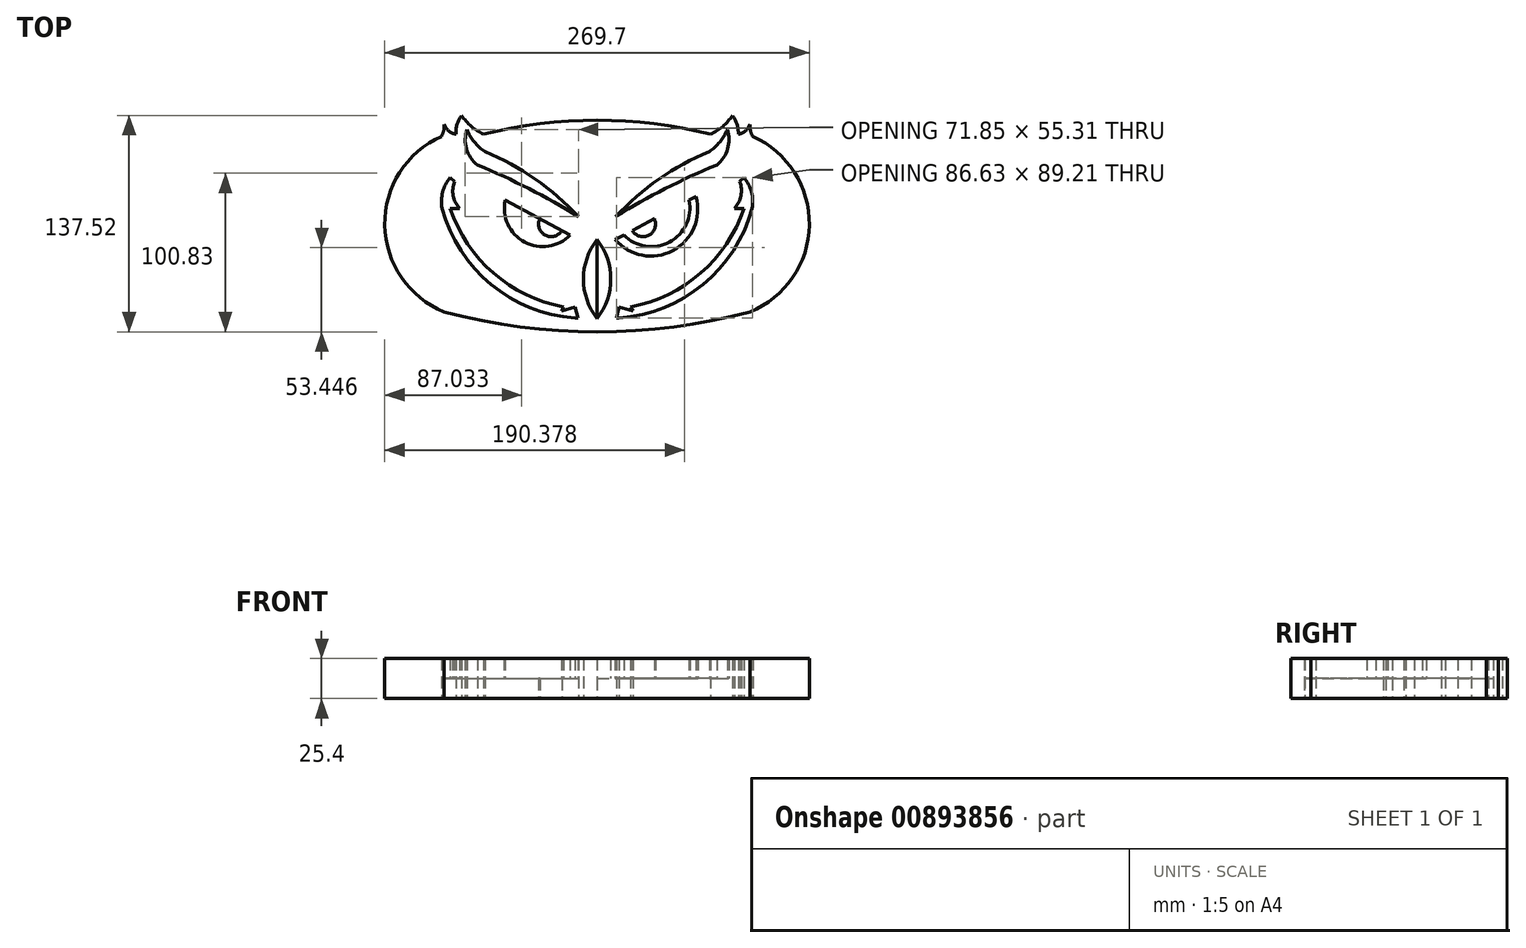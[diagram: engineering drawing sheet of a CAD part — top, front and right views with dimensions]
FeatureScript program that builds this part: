
annotation { "Feature Type Name" : "Feature", "Feature Type Description" : "" }
export const myFeature = defineFeature(function(context is Context, id is Id, definition is map)
    precondition{}
    {
        {
            var Q0;
            Q0=qCreatedBy(makeId("Top.planeOp"),FACE);
            var sketch = newSketch(context, id + "F0", { "sketchPlane" : qUnion([Q0])});
            skLineSegment(sketch, "E0", {"start": v(0, 1.57) * mm, "end": v(0, 56.87) * mm});
            skLineSegment(sketch, "E1", {"start": v(0, 56.87) * mm, "end": v(0, -60.2) * mm});
            skArc(sketch, "E2", {"start": v(72, 56.87) * mm, "mid": v(79.84, 61.88) * mm, "end": v(86, 68.86) * mm});
            skArc(sketch, "E3", {"start": v(89.69, 56.87) * mm, "mid": v(88.87, 63.18) * mm, "end": v(86, 68.86) * mm});
            skArc(sketch, "E4", {"start": v(89.69, 56.87) * mm, "mid": v(94.25, 58.98) * mm, "end": v(97.06, 63.14) * mm});
            skArc(sketch, "E5", {"start": v(97.06, 63.14) * mm, "mid": v(97.42, 59.14) * mm, "end": v(98.9, 55.4) * mm});
            skArc(sketch, "E6", {"start": v(97.06, -55.95) * mm, "mid": v(134.84, -0.89) * mm, "end": v(98.9, 55.4) * mm});
            skArc(sketch, "E7", {"start": v(71.25, 45.81) * mm, "mid": v(77.96, 52) * mm, "end": v(82.68, 59.82) * mm});
            skArc(sketch, "E8", {"start": v(71.25, 45.81) * mm, "mid": v(39.29, 28.45) * mm, "end": v(11.9, 4.52) * mm});
            skArc(sketch, "E9", {"start": v(76.05, 37.33) * mm, "mid": v(43.27, 22.3) * mm, "end": v(11.9, 4.52) * mm});
            skArc(sketch, "E10", {"start": v(76.05, 37.33) * mm, "mid": v(82.91, 47.53) * mm, "end": v(82.68, 59.82) * mm});
            skLineSegment(sketch, "E11", {"start": v(11.52, -10.05) * mm, "end": v(83.79, 28.48) * mm});
            skArc(sketch, "E12", {"start": v(11.52, -10.05) * mm, "mid": v(48.19, -17.02) * mm, "end": v(62.83, 17.3) * mm});
            skArc(sketch, "E13", {"start": v(17.05, -7.1) * mm, "mid": v(46.02, -11.63) * mm, "end": v(58.4, 14.94) * mm});
            skArc(sketch, "E14", {"start": v(22.37, -4.26) * mm, "mid": v(32.92, -7.25) * mm, "end": v(36.33, 3.18) * mm});
            skArc(sketch, "E15", {"start": v(0, -60.2) * mm, "mid": v(8.68, -35.12) * mm, "end": v(0, -10.05) * mm});
            skArc(sketch, "E16.MirrorCS", {"start": v(-72, 56.87) * mm, "mid": v(-79.84, 61.88) * mm, "end": v(-86, 68.86) * mm});
            skArc(sketch, "E17.MirrorCS", {"start": v(-89.69, 56.87) * mm, "mid": v(-88.87, 63.18) * mm, "end": v(-86, 68.86) * mm});
            skArc(sketch, "E18.MirrorCS", {"start": v(-89.69, 56.87) * mm, "mid": v(-94.25, 58.98) * mm, "end": v(-97.06, 63.14) * mm});
            skArc(sketch, "E19.MirrorCS", {"start": v(-97.06, 63.14) * mm, "mid": v(-97.42, 59.14) * mm, "end": v(-98.9, 55.4) * mm});
            skArc(sketch, "E20.MirrorCS", {"start": v(-97.06, -55.95) * mm, "mid": v(-134.84, -0.89) * mm, "end": v(-98.9, 55.4) * mm});
            skArc(sketch, "E21.MirrorCS", {"start": v(0, -60.2) * mm, "mid": v(-8.68, -35.12) * mm, "end": v(0, -10.05) * mm});
            skArc(sketch, "E22.MirrorCS", {"start": v(-11.52, -10.05) * mm, "mid": v(-48.19, -17.02) * mm, "end": v(-62.83, 17.3) * mm});
            skArc(sketch, "E23.MirrorCS", {"start": v(-17.05, -7.1) * mm, "mid": v(-46.02, -11.63) * mm, "end": v(-58.4, 14.94) * mm});
            skArc(sketch, "E24.MirrorCS", {"start": v(-22.37, -4.26) * mm, "mid": v(-32.92, -7.25) * mm, "end": v(-36.33, 3.18) * mm});
            skArc(sketch, "E25.MirrorCS", {"start": v(-71.25, 45.81) * mm, "mid": v(-39.29, 28.45) * mm, "end": v(-11.9, 4.52) * mm});
            skArc(sketch, "E26.MirrorCS", {"start": v(-76.05, 37.33) * mm, "mid": v(-43.27, 22.3) * mm, "end": v(-11.9, 4.52) * mm});
            skArc(sketch, "E27.MirrorCS", {"start": v(-76.05, 37.33) * mm, "mid": v(-82.91, 47.53) * mm, "end": v(-82.68, 59.82) * mm});
            skArc(sketch, "E28.MirrorCS", {"start": v(-71.25, 45.81) * mm, "mid": v(-77.96, 52) * mm, "end": v(-82.68, 59.82) * mm});
            skArc(sketch, "E29", {"start": v(72, 56.87) * mm, "mid": v(0, 65.72) * mm, "end": v(-72, 56.87) * mm});
            skArc(sketch, "E30", {"start": v(-97.06, -55.95) * mm, "mid": v(0, -68.66) * mm, "end": v(97.06, -55.95) * mm});
            skLineSegment(sketch, "E31", {"start": v(-11.03, -68.5) * mm, "end": v(0, -78.07) * mm});
            skLineSegment(sketch, "E32", {"start": v(0, -78.07) * mm, "end": v(8.26, -68.57) * mm});
            skArc(sketch, "E33", {"start": v(-98.44, 9.8) * mm, "mid": v(-67.42, -38.53) * mm, "end": v(-14.09, -59.82) * mm});
            skLineSegment(sketch, "E34", {"start": v(-62.83, 17.3) * mm, "end": v(-11.52, -10.05) * mm});
            skArc(sketch, "E35", {"start": v(-93.22, 29.39) * mm, "mid": v(-98.07, 20.19) * mm, "end": v(-98.44, 9.8) * mm});
            skLineSegment(sketch, "E36", {"start": v(-93.22, 29.39) * mm, "end": v(-90.6, 26.78) * mm});
            skArc(sketch, "E37", {"start": v(-90.6, 26.78) * mm, "mid": v(-91.34, 17.8) * mm, "end": v(-87.25, 9.8) * mm});
            skLineSegment(sketch, "E38", {"start": v(-87.25, 9.8) * mm, "end": v(-93.22, 9.8) * mm});
            skArc(sketch, "E39", {"start": v(-93.22, 9.8) * mm, "mid": v(-65.84, -31.3) * mm, "end": v(-21.37, -52.72) * mm});
            skLineSegment(sketch, "E40", {"start": v(-21.37, -52.72) * mm, "end": v(-22.68, -55.5) * mm});
            skLineSegment(sketch, "E41", {"start": v(-22.68, -55.5) * mm, "end": v(-14.09, -52.72) * mm});
            skLineSegment(sketch, "E42", {"start": v(-14.09, -52.72) * mm, "end": v(-12.21, -59.82) * mm});
            skLineSegment(sketch, "E43", {"start": v(-12.21, -59.82) * mm, "end": v(-14.09, -59.82) * mm});
            skArc(sketch, "E44.MirrorCS", {"start": v(90.6, 26.78) * mm, "mid": v(91.34, 17.8) * mm, "end": v(87.25, 9.8) * mm});
            skArc(sketch, "E45.MirrorCS", {"start": v(93.22, 29.39) * mm, "mid": v(98.07, 20.19) * mm, "end": v(98.44, 9.8) * mm});
            skLineSegment(sketch, "E46.MirrorCS", {"start": v(93.22, 29.39) * mm, "end": v(90.6, 26.78) * mm});
            skLineSegment(sketch, "E47.MirrorCS", {"start": v(87.25, 9.8) * mm, "end": v(93.22, 9.8) * mm});
            skArc(sketch, "E48.MirrorCS", {"start": v(93.22, 9.8) * mm, "mid": v(65.84, -31.3) * mm, "end": v(21.37, -52.72) * mm});
            skArc(sketch, "E49.MirrorCS", {"start": v(98.44, 9.8) * mm, "mid": v(67.42, -38.53) * mm, "end": v(14.09, -59.82) * mm});
            skLineSegment(sketch, "E50.MirrorCS", {"start": v(22.68, -55.5) * mm, "end": v(14.09, -52.72) * mm});
            skLineSegment(sketch, "E51.MirrorCS", {"start": v(21.37, -52.72) * mm, "end": v(22.68, -55.5) * mm});
            skLineSegment(sketch, "E52.MirrorCS", {"start": v(14.09, -52.72) * mm, "end": v(12.21, -59.82) * mm});
            skLineSegment(sketch, "E53.MirrorCS", {"start": v(12.21, -59.82) * mm, "end": v(14.09, -59.82) * mm});
            skSolve(sketch);
        }
        {
            var Q0;
            Q0=makeQuery(id+"F0.imprint","IMPRINT",FACE,{"disambiguationData":[TD([[makeQuery(id+"F0.imprint","IMPRINT",EDGE,{"derivedFrom":sQuery(id+"F0.wireOp",EDGE,"E2")}),-1.0]])]});
            var Q1;
            {var subQ0=sQuery(id+"F0.wireOp",EDGE,"E13");Q1=makeQuery(id+"F0.imprint","IMPRINT",FACE,{"disambiguationData":[TD([[makeQuery(id+"F0.imprint","IMPRINT",EDGE,{"derivedFrom":subQ0}),1.0]])]});}
            var Q2;
            {var subQ0=sQuery(id+"F0.wireOp",EDGE,"E23.MirrorCS");Q2=makeQuery(id+"F0.imprint","IMPRINT",FACE,{"disambiguationData":[TD([[makeQuery(id+"F0.imprint","IMPRINT",EDGE,{"derivedFrom":subQ0}),-1.0]])]});}
            extrude(context, id + "F1", {"entities" : qUnion([Q0, Q1, Q2]), "depth" : 25.4 * mm, "offsetDistance" : 25.4 * mm});
        }
        {
            var Q0;
            Q0=makeQuery(id+"F0.imprint","IMPRINT",FACE,{"disambiguationData":[TD([[makeQuery(id+"F0.imprint","IMPRINT",EDGE,{"derivedFrom":sQuery(id+"F0.wireOp",EDGE,"E33")}),1.0]])]});
            var Q1;
            Q1=makeQuery(id+"F0.imprint","IMPRINT",FACE,{"disambiguationData":[TD([[makeQuery(id+"F0.imprint","IMPRINT",EDGE,{"derivedFrom":sQuery(id+"F0.wireOp",EDGE,"E25.MirrorCS")}),-1.0]])]});
            var Q2;
            Q2=makeQuery(id+"F0.imprint","IMPRINT",FACE,{"disambiguationData":[TD([[makeQuery(id+"F0.imprint","IMPRINT",EDGE,{"derivedFrom":sQuery(id+"F0.wireOp",EDGE,"E7")}),-1.0]])]});
            var Q3;
            {var subQ0=sQuery(id+"F0.wireOp",EDGE,"E14");Q3=makeQuery(id+"F0.imprint","IMPRINT",FACE,{"disambiguationData":[TD([[makeQuery(id+"F0.imprint","IMPRINT",EDGE,{"derivedFrom":subQ0}),1.0]])]});}
            var Q4;
            {var subQ0=sQuery(id+"F0.wireOp",EDGE,"E12");Q4=makeQuery(id+"F0.imprint","IMPRINT",FACE,{"disambiguationData":[TD([[makeQuery(id+"F0.imprint","IMPRINT",EDGE,{"derivedFrom":subQ0}),1.0]])]});}
            var Q5;
            {var subQ0=sQuery(id+"F0.wireOp",EDGE,"E22.MirrorCS");Q5=makeQuery(id+"F0.imprint","IMPRINT",FACE,{"disambiguationData":[TD([[makeQuery(id+"F0.imprint","IMPRINT",EDGE,{"derivedFrom":subQ0}),-1.0]])]});}
            var Q6;
            {var subQ0=sQuery(id+"F0.wireOp",EDGE,"E24.MirrorCS");Q6=makeQuery(id+"F0.imprint","IMPRINT",FACE,{"disambiguationData":[TD([[makeQuery(id+"F0.imprint","IMPRINT",EDGE,{"derivedFrom":subQ0}),-1.0]])]});}
            var Q7;
            Q7=makeQuery(id+"F0.imprint","IMPRINT",FACE,{"disambiguationData":[TD([[makeQuery(id+"F0.imprint","IMPRINT",EDGE,{"derivedFrom":sQuery(id+"F0.wireOp",EDGE,"E44.MirrorCS")}),1.0]])]});
            var Q8;
            {var subQ1=sQuery(id+"F0.wireOp",EDGE,"E15");Q8=makeQuery(id+"F0.imprint","IMPRINT",FACE,{"disambiguationData":[TD([[makeQuery(id+"F0.imprint","IMPRINT",EDGE,{"derivedFrom":subQ1}),1.0]])]});}
            var Q9;
            {var subQ0=sQuery(id+"F0.wireOp",EDGE,"E21.MirrorCS");Q9=makeQuery(id+"F0.imprint","IMPRINT",FACE,{"disambiguationData":[TD([[makeQuery(id+"F0.imprint","IMPRINT",EDGE,{"derivedFrom":subQ0}),-1.0]])]});}
            extrude(context, id + "F2", {"entities" : qUnion([Q0, Q1, Q2, Q3, Q4, Q5, Q6, Q7, Q8, Q9]), "operationType" : NewBodyOperationType.ADD, "depth" : 12.7 * mm, "offsetDistance" : 25.4 * mm});
        }
    });
